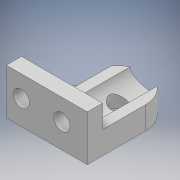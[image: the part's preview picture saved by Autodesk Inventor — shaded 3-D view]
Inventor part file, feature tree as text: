
AUTODESK INVENTOR PART (.ipt)
format: ipt  version: 2019.1 (Build 231200000, 200)  size: 171,520 bytes
history: native  units: mm
features: sketch x5, extrude x5
ambient origin geometry x8: Origin, YZ Plane, XZ Plane, XY Plane, X Axis, Y Axis, Z Axis, Center Point
bodies: Solid1 (feature_tree)
feature tree (10):
  sketch  "Sketch1"  dims[d9=4.5mm d10=0.0mm d11=4.5mm d12=0.0mm]
  extrude  "Extrusion1"  Depth=4.5mm TaperAngle=0.0deg
  extrude  "Extrusion2"  Depth=3.2mm
  extrude  "Extrusion3"  Depth=3.0mm
  extrude  "Extrusion4"  TaperAngle=90.0deg  [1 undecoded]
  extrude  "Extrusion5"  Depth=10.0mm
  sketch  "Sketch4"  dims[d13=3.2mm d14=3.2mm]
  sketch  "Sketch5"  dims[d15=5.5mm d16=0.0mm d17=3.0mm]
  sketch  "Sketch6"  dims[d19=11.5mm d23=90.0deg]
  sketch  "Sketch7"  dims[d25=12.5mm d31=5.5mm d32=150.0deg d34=6.0mm d35=6.0mm d36=10.0mm d37=0.0mm d38=4.8mm d39=4.8mm d40=4.8mm d41=4.8mm d42=10.0mm d43=0.0mm d46=2.75mm d47=0.0mm d49=3.2mm d50=8.0mm d51=18.0mm d52=5.0mm]
note: 1 required parameter value undecoded (feature->parameter linkage not recoverable at this tier; creation-order binding heuristic only, values carry confidence <= 0.55)
